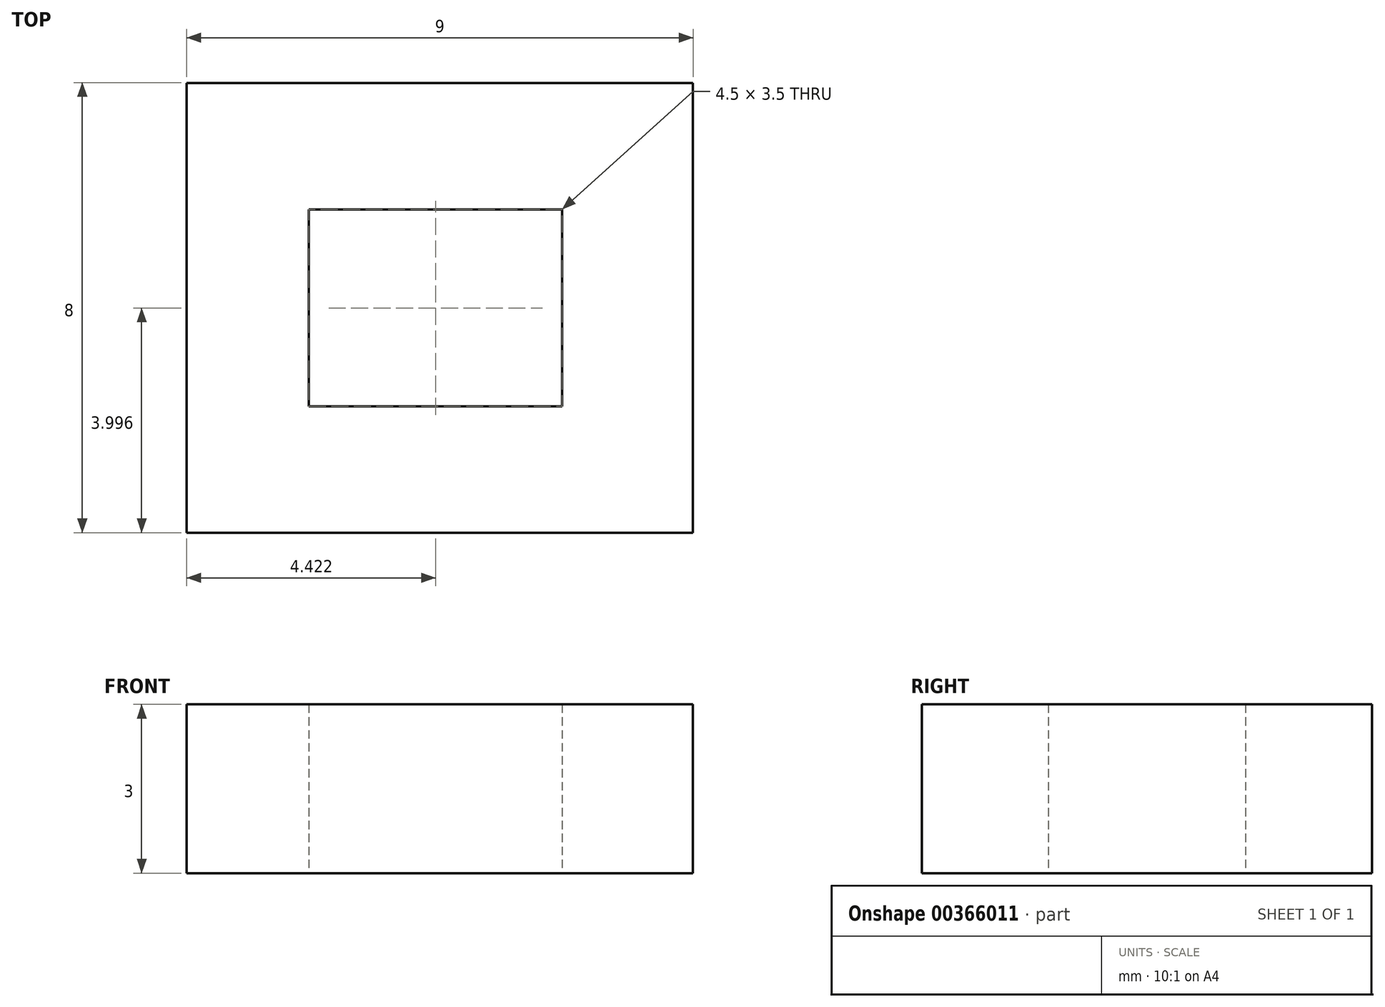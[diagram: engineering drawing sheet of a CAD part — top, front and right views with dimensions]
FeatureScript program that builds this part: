
annotation { "Feature Type Name" : "Feature", "Feature Type Description" : "" }
export const myFeature = defineFeature(function(context is Context, id is Id, definition is map)
    precondition{}
    {
        {
            var Q0;
            Q0=qCreatedBy(makeId("Top.planeOp"),FACE);
            var sketch = newSketch(context, id + "F0", { "sketchPlane" : qUnion([Q0])});
            skLineSegment(sketch, "E0.bottom", {"start": v(-3.21, 4.65) * mm, "end": v(5.79, 4.65) * mm});
            skLineSegment(sketch, "E0.top", {"start": v(-3.21, -3.35) * mm, "end": v(5.79, -3.35) * mm});
            skLineSegment(sketch, "E0.left", {"start": v(-3.21, 4.65) * mm, "end": v(-3.21, -3.35) * mm});
            skLineSegment(sketch, "E0.right", {"start": v(5.79, 4.65) * mm, "end": v(5.79, -3.35) * mm});
            skLineSegment(sketch, "E1.bottom", {"start": v(-1.04, 2.4) * mm, "end": v(3.46, 2.4) * mm});
            skLineSegment(sketch, "E1.top", {"start": v(-1.04, -1.1) * mm, "end": v(3.46, -1.1) * mm});
            skLineSegment(sketch, "E1.left", {"start": v(-1.04, 2.4) * mm, "end": v(-1.04, -1.1) * mm});
            skLineSegment(sketch, "E1.right", {"start": v(3.46, 2.4) * mm, "end": v(3.46, -1.1) * mm});
            skSolve(sketch);
        }
        {
            var Q0;
            Q0=makeQuery(id+"F0.imprint","IMPRINT",FACE,{"disambiguationData":[TD([[makeQuery(id+"F0.imprint","IMPRINT",EDGE,{"derivedFrom":sQuery(id+"F0.wireOp",EDGE,"E0.bottom")}),-1.0]])]});
            extrude(context, id + "F1", {"entities" : qUnion([Q0]), "depth" : 3 * mm});
        }
    });
